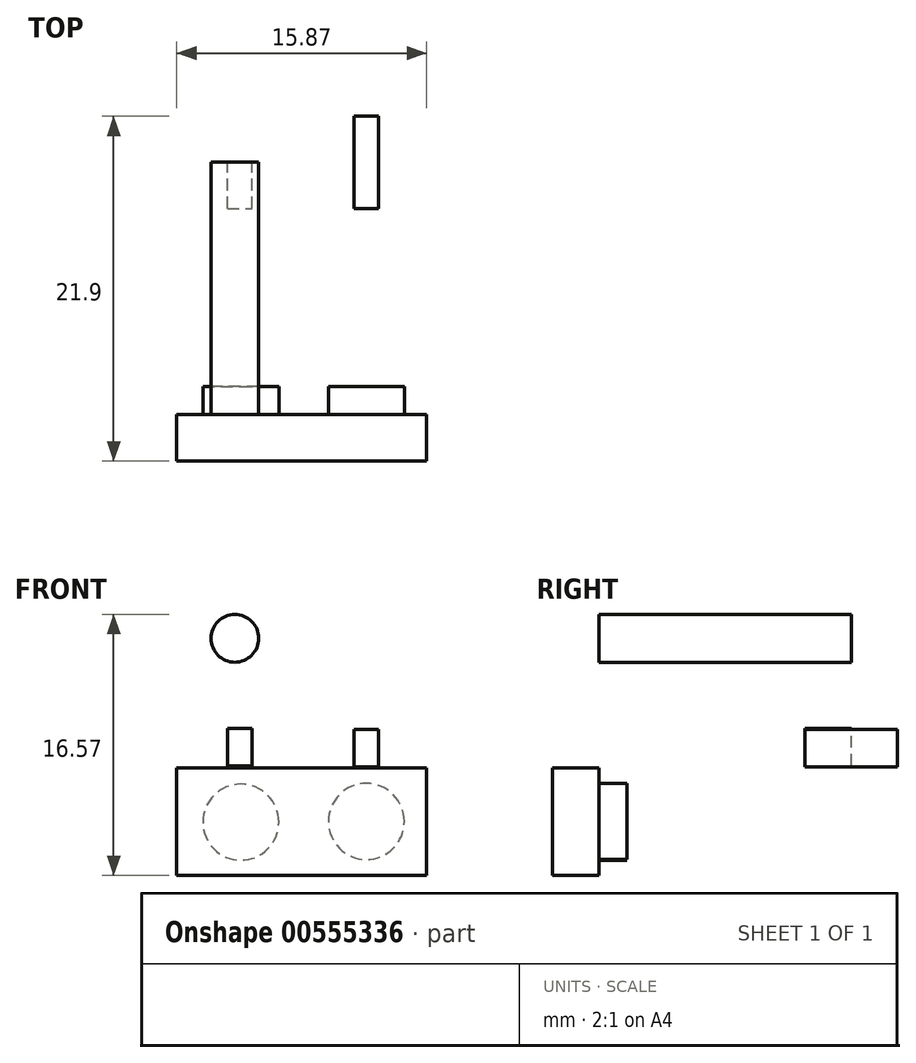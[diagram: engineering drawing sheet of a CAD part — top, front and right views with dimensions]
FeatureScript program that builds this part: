
annotation { "Feature Type Name" : "Feature", "Feature Type Description" : "" }
export const myFeature = defineFeature(function(context is Context, id is Id, definition is map)
    precondition{}
    {
        {
            var Q0;
            Q0=qCreatedBy(makeId("Front.planeOp"),FACE);
            var sketch = newSketch(context, id + "F0", { "sketchPlane" : qUnion([Q0])});
            skLineSegment(sketch, "E0.bottom", {"start": v(0, 0) * mm, "end": v(-15.87, 0) * mm});
            skLineSegment(sketch, "E0.top", {"start": v(0, 6.82) * mm, "end": v(-15.87, 6.82) * mm});
            skLineSegment(sketch, "E0.left", {"start": v(0, 0) * mm, "end": v(0, 6.82) * mm});
            skLineSegment(sketch, "E0.right", {"start": v(-15.87, 0) * mm, "end": v(-15.87, 6.82) * mm});
            skSolve(sketch);
        }
        {
            var Q0;
            Q0=makeQuery(id+"F0.imprint","IMPRINT",FACE,{"disambiguationData":[TD([[makeQuery(id+"F0.imprint","IMPRINT",EDGE,{"derivedFrom":sQuery(id+"F0.wireOp",EDGE,"E0.bottom")}),-1.0]])]});
            extrude(context, id + "F1", {"entities" : qUnion([Q0]), "depth" : 2.94 * mm, "offsetDistance" : 25 * mm});
        }
        {
            var Q0;
            Q0=qCreatedBy(makeId("Front.planeOp"),FACE);
            var sketch = newSketch(context, id + "F2", { "sketchPlane" : qUnion([Q0])});
            skCircle(sketch, "E1", {"center": v(-11.8, 3.38) * mm, "radius": 2.42 * mm});
            skCircle(sketch, "E2", {"center": v(-3.83, 3.42) * mm, "radius": 2.42 * mm});
            skSolve(sketch);
        }
        {
            var Q0;
            Q0 = qSketchRegion(id + "F2", true);
            extrude(context, id + "F3", {"entities" : qUnion([Q0]), "operationType" : NewBodyOperationType.ADD, "oppositeDirection" : true, "depth" : (1.78) * mm, "offsetDistance" : 25 * mm});
        }
        {
            var Q0;
            Q0=qCreatedBy(makeId("Front.planeOp"),FACE);
            var sketch = newSketch(context, id + "F4", { "sketchPlane" : qUnion([Q0])});
            skCircle(sketch, "E3", {"center": v(-12.18, 15.05) * mm, "radius": 1.51 * mm});
            skSolve(sketch);
        }
        {
            var Q0;
            Q0=makeQuery(id+"F4.imprint","IMPRINT",FACE,{"disambiguationData":[TD([[makeQuery(id+"F4.imprint","IMPRINT",EDGE,{"derivedFrom":sQuery(id+"F4.wireOp",EDGE,"E3")}),1.0]])]});
            var Q1;
            Q1=sQuery(id+"F4.wireOp",EDGE,"E3");
            extrude(context, id + "F5", {"entities" : qUnion([Q0]), "surfaceEntities" : qUnion([Q1]), "oppositeDirection" : true, "depth" : 16.03 * mm, "offsetDistance" : 25 * mm});
        }
        {
            var Q0;
            Q0=makeQuery(id+"F5.opExtrude","CAP_FACE",FACE,{"disambiguationData":[OSD([sQuery(id+"F4.wireOp",EDGE,"E3")])],"isStart":false});
            var sketch = newSketch(context, id + "F6", { "sketchPlane" : qUnion([Q0])});
            skLineSegment(sketch, "E4.bottom", {"start": v(4.62, 6.88) * mm, "end": v(3.07, 6.88) * mm});
            skLineSegment(sketch, "E4.top", {"start": v(4.62, 9.26) * mm, "end": v(3.07, 9.26) * mm});
            skLineSegment(sketch, "E4.left", {"start": v(3.07, 6.88) * mm, "end": v(3.07, 9.26) * mm});
            skLineSegment(sketch, "E4.right", {"start": v(4.62, 6.88) * mm, "end": v(4.62, 9.26) * mm});
            skLineSegment(sketch, "E5.bottom", {"start": v(12.65, 6.96) * mm, "end": v(11.08, 6.96) * mm});
            skLineSegment(sketch, "E5.top", {"start": v(12.65, 9.34) * mm, "end": v(11.08, 9.34) * mm});
            skLineSegment(sketch, "E5.left", {"start": v(12.65, 6.96) * mm, "end": v(12.65, 9.34) * mm});
            skLineSegment(sketch, "E5.right", {"start": v(11.08, 6.96) * mm, "end": v(11.08, 9.34) * mm});
            skSolve(sketch);
        }
        {
            var Q0;
            Q0=makeQuery(id+"F6.imprint","IMPRINT",FACE,{"disambiguationData":[TD([[makeQuery(id+"F6.imprint","IMPRINT",EDGE,{"derivedFrom":sQuery(id+"F6.wireOp",EDGE,"E4.bottom")}),-1.0]])]});
            var Q1;
            Q1=qCreatedBy(makeId("Front.planeOp"),FACE);
            extrude(context, id + "F7", {"entities" : qUnion([Q0]), "depth" : 2.93 * mm, "endBoundEntityFace" : qUnion([Q1]), "offsetDistance" : 25 * mm});
        }
        {
            var Q0;
            Q0=makeQuery(id+"F6.imprint","IMPRINT",FACE,{"disambiguationData":[TD([[makeQuery(id+"F6.imprint","IMPRINT",EDGE,{"derivedFrom":sQuery(id+"F6.wireOp",EDGE,"E5.bottom")}),-1.0]])]});
            var Q1;
            Q1=makeQuery(id+"F6.imprint","IMPRINT",FACE,{"disambiguationData":[TD([[makeQuery(id+"F6.imprint","IMPRINT",EDGE,{"derivedFrom":sQuery(id+"F6.wireOp",EDGE,"E4.bottom")}),-1.0]])]});
            extrude(context, id + "F8", {"entities" : qUnion([Q0, Q1]), "operationType" : NewBodyOperationType.ADD, "oppositeDirection" : true, "depth" : 2.94 * mm, "offsetDistance" : 25 * mm});
        }
    });
